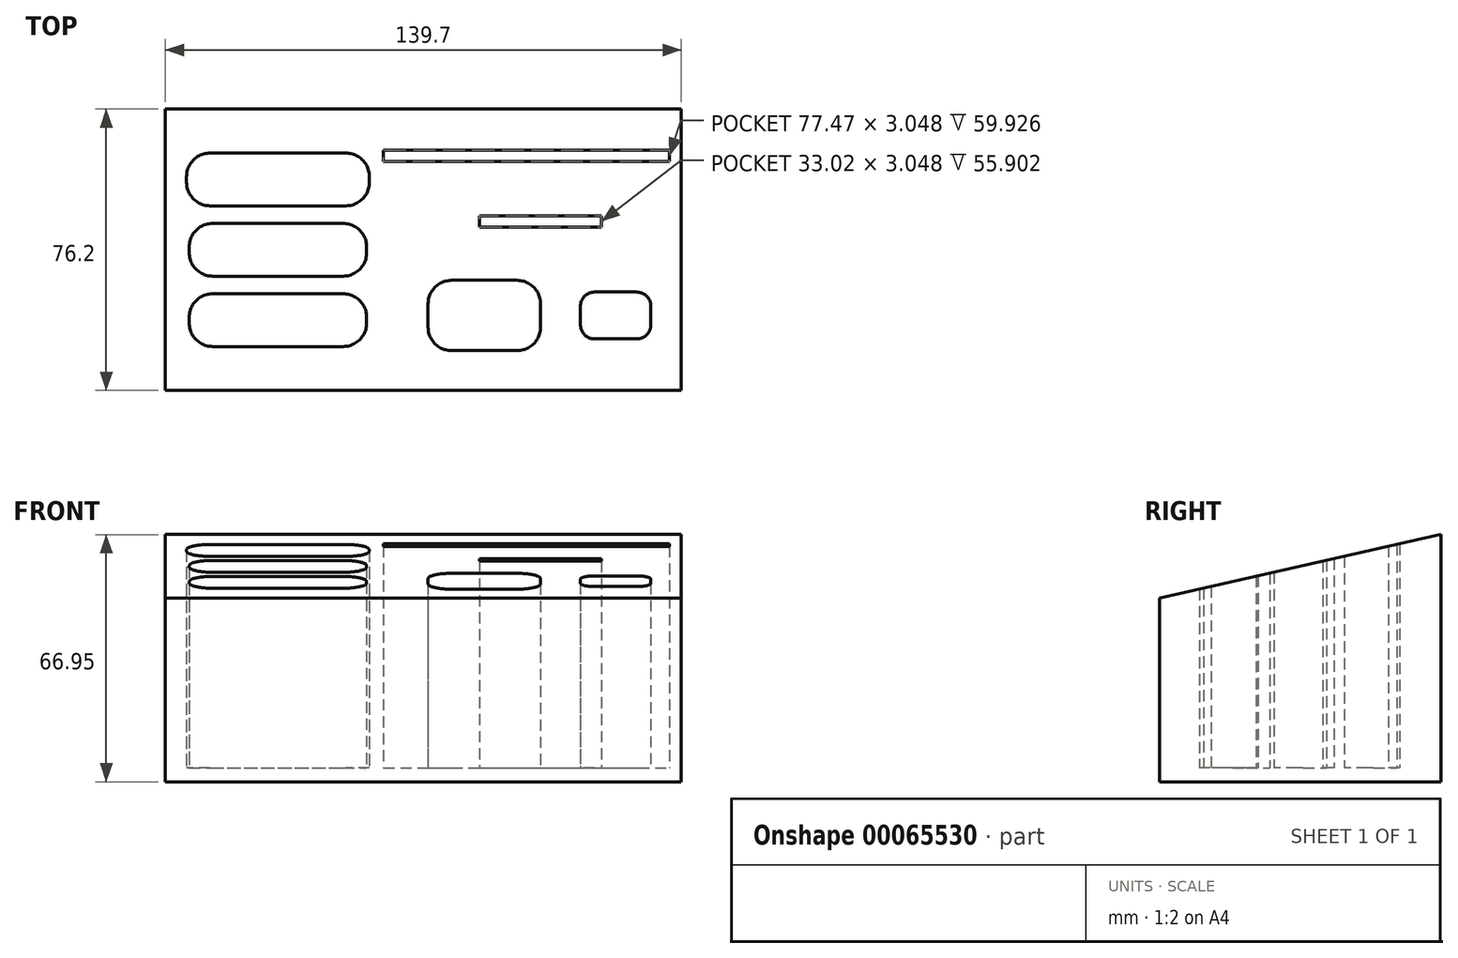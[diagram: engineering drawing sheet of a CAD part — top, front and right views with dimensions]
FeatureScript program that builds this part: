
annotation { "Feature Type Name" : "Feature", "Feature Type Description" : "" }
export const myFeature = defineFeature(function(context is Context, id is Id, definition is map)
    precondition{}
    {
        {
            var Q0;
            Q0=qCreatedBy(makeId("Top.planeOp"),FACE);
            var sketch = newSketch(context, id + "F0", { "sketchPlane" : qUnion([Q0])});
            skLineSegment(sketch, "E0.rect.bottom", {"start": v(-69.85, 38.1) * mm, "end": v(69.85, 38.1) * mm});
            skLineSegment(sketch, "E0.rect.top", {"start": v(-69.85, -38.1) * mm, "end": v(69.85, -38.1) * mm});
            skLineSegment(sketch, "E0.rect.left", {"start": v(-69.85, 38.1) * mm, "end": v(-69.85, -38.1) * mm});
            skLineSegment(sketch, "E0.rect.right", {"start": v(69.85, 38.1) * mm, "end": v(69.85, -38.1) * mm});
            skPoint(sketch, "E0.rect.middle", {"position": v(0, 0) * mm});
            skLineSegment(sketch, "E1.rect.bottom", {"start": v(-57.04, -11.9) * mm, "end": v(-21.7, -11.9) * mm});
            skLineSegment(sketch, "E1.rect.top", {"start": v(-57.04, -26.2) * mm, "end": v(-21.7, -26.2) * mm});
            skLineSegment(sketch, "E1.rect.left", {"start": v(-63.4, -18.26) * mm, "end": v(-63.4, -19.84) * mm});
            skLineSegment(sketch, "E1.rect.right", {"start": v(-15.35, -18.26) * mm, "end": v(-15.35, -19.84) * mm});
            skPoint(sketch, "E1.rect.middle", {"position": v(-39.37, -19.05) * mm});
            skLineSegment(sketch, "E2.rect.bottom", {"start": v(-57.04, 7.14) * mm, "end": v(-21.7, 7.14) * mm});
            skLineSegment(sketch, "E2.rect.top", {"start": v(-57.04, -7.14) * mm, "end": v(-21.7, -7.14) * mm});
            skLineSegment(sketch, "E2.rect.left", {"start": v(-63.4, 0.8) * mm, "end": v(-63.4, -0.8) * mm});
            skLineSegment(sketch, "E2.rect.right", {"start": v(-15.35, 0.8) * mm, "end": v(-15.35, -0.8) * mm});
            skPoint(sketch, "E2.rect.middle", {"position": v(-39.37, 0) * mm});
            skLineSegment(sketch, "E3.rect.bottom", {"start": v(-57.78, 26.2) * mm, "end": v(-20.96, 26.2) * mm});
            skLineSegment(sketch, "E3.rect.top", {"start": v(-57.78, 11.9) * mm, "end": v(-20.96, 11.9) * mm});
            skLineSegment(sketch, "E3.rect.left", {"start": v(-64.13, 19.84) * mm, "end": v(-64.13, 18.26) * mm});
            skLineSegment(sketch, "E3.rect.right", {"start": v(-14.6, 19.84) * mm, "end": v(-14.6, 18.26) * mm});
            skPoint(sketch, "E3.rect.middle", {"position": v(-39.37, 19.05) * mm});
            skPoint(sketch, "E4.endSnap0", {"position": v(-14.6, 19.05) * mm});
            skPoint(sketch, "E5.end.orphan", {"position": v(-39.37, -9.52) * mm});
            skPoint(sketch, "E6.endSnap0", {"position": v(69.85, 0) * mm});
            skLineSegment(sketch, "E7.rect.bottom", {"start": v(-10.8, 26.92) * mm, "end": v(66.68, 26.92) * mm});
            skLineSegment(sketch, "E7.rect.top", {"start": v(-10.8, 23.88) * mm, "end": v(66.68, 23.88) * mm});
            skLineSegment(sketch, "E7.rect.left", {"start": v(-10.8, 26.92) * mm, "end": v(-10.8, 23.88) * mm});
            skLineSegment(sketch, "E7.rect.right", {"start": v(66.68, 26.92) * mm, "end": v(66.68, 23.88) * mm});
            skPoint(sketch, "E7.rect.middle", {"position": v(27.94, 25.4) * mm});
            skLineSegment(sketch, "E8.rect.bottom", {"start": v(15.24, 9.14) * mm, "end": v(48.26, 9.14) * mm});
            skLineSegment(sketch, "E8.rect.top", {"start": v(15.24, 6.1) * mm, "end": v(48.26, 6.1) * mm});
            skLineSegment(sketch, "E8.rect.left", {"start": v(15.24, 9.14) * mm, "end": v(15.24, 6.1) * mm});
            skLineSegment(sketch, "E8.rect.right", {"start": v(48.26, 9.14) * mm, "end": v(48.26, 6.1) * mm});
            skPoint(sketch, "E8.rect.middle", {"position": v(31.75, 7.62) * mm});
            skLineSegment(sketch, "E9.rect.bottom", {"start": v(46.35, -11.43) * mm, "end": v(57.78, -11.43) * mm});
            skLineSegment(sketch, "E9.rect.top", {"start": v(46.35, -24.13) * mm, "end": v(57.78, -24.13) * mm});
            skLineSegment(sketch, "E9.rect.left", {"start": v(42.54, -15.24) * mm, "end": v(42.54, -20.32) * mm});
            skLineSegment(sketch, "E9.rect.right", {"start": v(61.6, -15.24) * mm, "end": v(61.6, -20.32) * mm});
            skPoint(sketch, "E9.rect.middle", {"position": v(52.07, -17.78) * mm});
            skLineSegment(sketch, "E10.rect.bottom", {"start": v(7.62, -8.25) * mm, "end": v(25.4, -8.25) * mm});
            skLineSegment(sketch, "E10.rect.top", {"start": v(7.62, -27.3) * mm, "end": v(25.4, -27.3) * mm});
            skLineSegment(sketch, "E10.rect.left", {"start": v(1.27, -14.6) * mm, "end": v(1.27, -20.95) * mm});
            skLineSegment(sketch, "E10.rect.right", {"start": v(31.75, -14.6) * mm, "end": v(31.75, -20.95) * mm});
            skPoint(sketch, "E10.rect.middle", {"position": v(16.5, -17.78) * mm});
            skPoint(sketch, "E11.visualSharp", {"position": v(1.27, -8.25) * mm});
            skArc(sketch, "E11.filletArc", {"start": v(7.62, -8.25) * mm, "mid": v(3.13, -10.11) * mm, "end": v(1.27, -14.6) * mm});
            skPoint(sketch, "E12.visualSharp", {"position": v(1.27, -27.3) * mm});
            skArc(sketch, "E12.filletArc", {"start": v(1.27, -20.95) * mm, "mid": v(3.13, -25.45) * mm, "end": v(7.62, -27.3) * mm});
            skPoint(sketch, "E13.visualSharp", {"position": v(31.75, -27.3) * mm});
            skArc(sketch, "E13.filletArc", {"start": v(25.4, -27.3) * mm, "mid": v(29.9, -25.45) * mm, "end": v(31.75, -20.95) * mm});
            skPoint(sketch, "E14.visualSharp", {"position": v(31.75, -8.25) * mm});
            skArc(sketch, "E14.filletArc", {"start": v(31.75, -14.6) * mm, "mid": v(29.9, -10.11) * mm, "end": v(25.4, -8.25) * mm});
            skPoint(sketch, "E15.visualSharp", {"position": v(-14.6, 11.9) * mm});
            skArc(sketch, "E15.filletArc", {"start": v(-20.96, 11.9) * mm, "mid": v(-16.47, 13.77) * mm, "end": v(-14.6, 18.26) * mm});
            skPoint(sketch, "E16.visualSharp", {"position": v(-14.6, 26.2) * mm});
            skArc(sketch, "E16.filletArc", {"start": v(-14.6, 19.84) * mm, "mid": v(-16.47, 24.33) * mm, "end": v(-20.96, 26.2) * mm});
            skPoint(sketch, "E17.visualSharp", {"position": v(-15.35, 7.14) * mm});
            skArc(sketch, "E17.filletArc", {"start": v(-15.35, 0.8) * mm, "mid": v(-17.2, 5.28) * mm, "end": v(-21.7, 7.14) * mm});
            skPoint(sketch, "E18.visualSharp", {"position": v(-15.35, -7.14) * mm});
            skArc(sketch, "E18.filletArc", {"start": v(-21.7, -7.14) * mm, "mid": v(-17.2, -5.28) * mm, "end": v(-15.35, -0.8) * mm});
            skPoint(sketch, "E19.visualSharp", {"position": v(-64.13, 26.2) * mm});
            skArc(sketch, "E19.filletArc", {"start": v(-57.78, 26.2) * mm, "mid": v(-62.27, 24.33) * mm, "end": v(-64.13, 19.84) * mm});
            skPoint(sketch, "E20.visualSharp", {"position": v(-64.13, 11.9) * mm});
            skArc(sketch, "E20.filletArc", {"start": v(-64.13, 18.26) * mm, "mid": v(-62.27, 13.77) * mm, "end": v(-57.78, 11.9) * mm});
            skPoint(sketch, "E21.visualSharp", {"position": v(-63.4, 7.14) * mm});
            skArc(sketch, "E21.filletArc", {"start": v(-57.04, 7.14) * mm, "mid": v(-61.53, 5.28) * mm, "end": v(-63.4, 0.8) * mm});
            skPoint(sketch, "E22.visualSharp", {"position": v(-63.4, -7.14) * mm});
            skArc(sketch, "E22.filletArc", {"start": v(-63.4, -0.8) * mm, "mid": v(-61.53, -5.28) * mm, "end": v(-57.04, -7.14) * mm});
            skPoint(sketch, "E23.visualSharp", {"position": v(-63.4, -11.9) * mm});
            skArc(sketch, "E23.filletArc", {"start": v(-57.04, -11.9) * mm, "mid": v(-61.53, -13.77) * mm, "end": v(-63.4, -18.26) * mm});
            skPoint(sketch, "E24.visualSharp", {"position": v(-63.4, -26.2) * mm});
            skArc(sketch, "E24.filletArc", {"start": v(-63.4, -19.84) * mm, "mid": v(-61.53, -24.33) * mm, "end": v(-57.04, -26.2) * mm});
            skPoint(sketch, "E25.visualSharp", {"position": v(-15.35, -26.2) * mm});
            skArc(sketch, "E25.filletArc", {"start": v(-21.7, -26.2) * mm, "mid": v(-17.2, -24.33) * mm, "end": v(-15.35, -19.84) * mm});
            skPoint(sketch, "E26.visualSharp", {"position": v(-15.35, -11.9) * mm});
            skArc(sketch, "E26.filletArc", {"start": v(-15.35, -18.26) * mm, "mid": v(-17.2, -13.77) * mm, "end": v(-21.7, -11.9) * mm});
            skPoint(sketch, "E27.visualSharp", {"position": v(61.6, -11.43) * mm});
            skArc(sketch, "E27.filletArc", {"start": v(61.6, -15.24) * mm, "mid": v(60.48, -12.55) * mm, "end": v(57.78, -11.43) * mm});
            skPoint(sketch, "E28.visualSharp", {"position": v(42.54, -11.43) * mm});
            skArc(sketch, "E28.filletArc", {"start": v(46.35, -11.43) * mm, "mid": v(43.66, -12.55) * mm, "end": v(42.54, -15.24) * mm});
            skPoint(sketch, "E29.visualSharp", {"position": v(42.54, -24.13) * mm});
            skArc(sketch, "E29.filletArc", {"start": v(42.54, -20.32) * mm, "mid": v(43.66, -23.01) * mm, "end": v(46.35, -24.13) * mm});
            skPoint(sketch, "E30.visualSharp", {"position": v(61.6, -24.13) * mm});
            skArc(sketch, "E30.filletArc", {"start": v(57.78, -24.13) * mm, "mid": v(60.48, -23.01) * mm, "end": v(61.6, -20.32) * mm});
            skSolve(sketch);
        }
        {
            var Q0;
            Q0=makeQuery(id+"F0.imprint","IMPRINT",FACE,{"disambiguationData":[TD([[makeQuery(id+"F0.imprint","IMPRINT",EDGE,{"derivedFrom":sQuery(id+"F0.wireOp",EDGE,"E0.rect.bottom")}),-1.0]])]});
            extrude(context, id + "F1", {"entities" : qUnion([Q0]), "depth" : 76.2 * mm});
        }
        {
            var Q0;
            Q0=makeQuery(id+"F1.opExtrude","SWEPT_FACE",FACE,{"disambiguationData":[OSD([sQuery(id+"F0.wireOp",EDGE,"E0.rect.left")])]});
            var sketch = newSketch(context, id + "F2", { "sketchPlane" : qUnion([Q0])});
            skLineSegment(sketch, "E31", {"start": v(-38.1, 66.95) * mm, "end": v(38.1, 49.71) * mm});
            skSolve(sketch);
        }
        {
            var Q0;
            Q0=makeQuery(id+"F0.imprint","IMPRINT",FACE,{"disambiguationData":[TD([[makeQuery(id+"F0.imprint","IMPRINT",EDGE,{"derivedFrom":sQuery(id+"F0.wireOp",EDGE,"E3.rect.bottom")}),-1.0]])]});
            var Q1;
            Q1=makeQuery(id+"F0.imprint","IMPRINT",FACE,{"disambiguationData":[TD([[makeQuery(id+"F0.imprint","IMPRINT",EDGE,{"derivedFrom":sQuery(id+"F0.wireOp",EDGE,"E2.rect.bottom")}),-1.0]])]});
            var Q2;
            Q2=makeQuery(id+"F0.imprint","IMPRINT",FACE,{"disambiguationData":[TD([[makeQuery(id+"F0.imprint","IMPRINT",EDGE,{"derivedFrom":sQuery(id+"F0.wireOp",EDGE,"E1.rect.bottom")}),-1.0]])]});
            var Q3;
            Q3=makeQuery(id+"F0.imprint","IMPRINT",FACE,{"disambiguationData":[TD([[makeQuery(id+"F0.imprint","IMPRINT",EDGE,{"derivedFrom":sQuery(id+"F0.wireOp",EDGE,"E10.rect.bottom")}),-1.0]])]});
            var Q4;
            Q4=makeQuery(id+"F0.imprint","IMPRINT",FACE,{"disambiguationData":[TD([[makeQuery(id+"F0.imprint","IMPRINT",EDGE,{"derivedFrom":sQuery(id+"F0.wireOp",EDGE,"E9.rect.bottom")}),-1.0]])]});
            var Q5;
            Q5=makeQuery(id+"F0.imprint","IMPRINT",FACE,{"disambiguationData":[TD([[makeQuery(id+"F0.imprint","IMPRINT",EDGE,{"derivedFrom":sQuery(id+"F0.wireOp",EDGE,"E8.rect.bottom")}),-1.0]])]});
            var Q6;
            Q6=makeQuery(id+"F0.imprint","IMPRINT",FACE,{"disambiguationData":[TD([[makeQuery(id+"F0.imprint","IMPRINT",EDGE,{"derivedFrom":sQuery(id+"F0.wireOp",EDGE,"E7.rect.bottom")}),-1.0]])]});
            extrude(context, id + "F3", {"entities" : qUnion([Q0, Q1, Q2, Q3, Q4, Q5, Q6]), "operationType" : NewBodyOperationType.ADD, "depth" : 3.8 * mm});
        }
        {
            var Q0;
            {var subQ0=sQuery(id+"F2.wireOp",EDGE,"E31");Q0=makeQuery(id+"F2.imprint","IMPRINT",FACE,{"disambiguationData":[TD([[makeQuery(id+"F2.imprint","IMPRINT",EDGE,{"derivedFrom":subQ0}),1.0]])]});}
            extrude(context, id + "F4", {"entities" : qUnion([Q0]), "operationType" : NewBodyOperationType.REMOVE, "endBound" : BoundingType.THROUGH_ALL, "oppositeDirection" : true, "depth" : 25.4 * mm});
        }
    });
